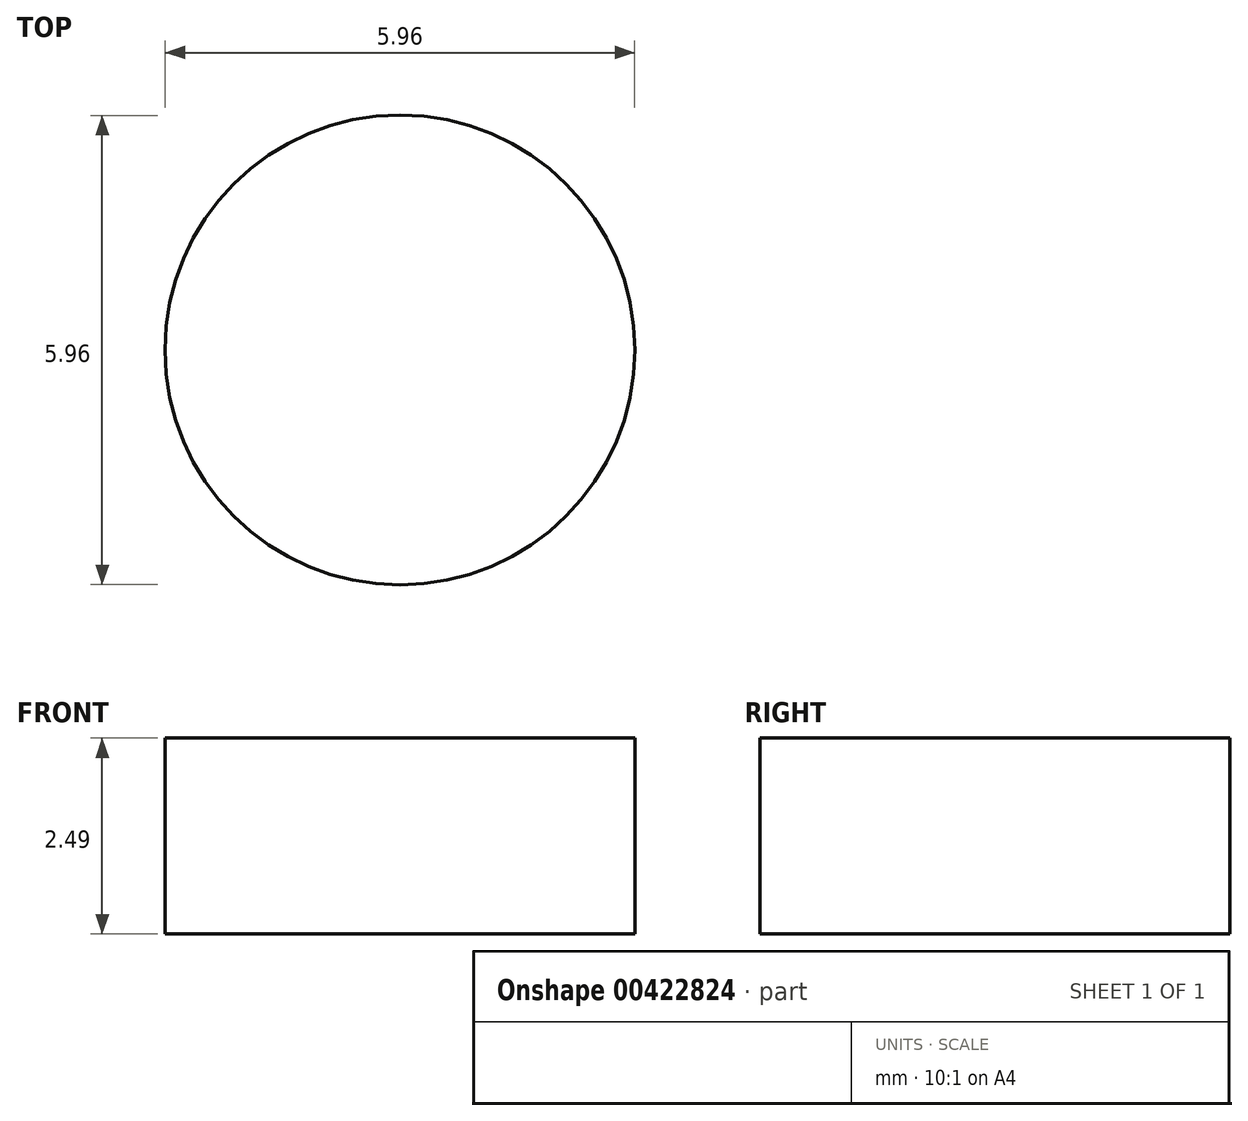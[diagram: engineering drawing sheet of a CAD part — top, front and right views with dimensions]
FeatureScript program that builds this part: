
annotation { "Feature Type Name" : "Feature", "Feature Type Description" : "" }
export const myFeature = defineFeature(function(context is Context, id is Id, definition is map)
    precondition{}
    {
        {
            var Q0;
            Q0=qCreatedBy(makeId("Top.planeOp"),FACE);
            var sketch = newSketch(context, id + "F0", { "sketchPlane" : qUnion([Q0])});
            skCircle(sketch, "E0", {"center": v(0, 0) * mm, "radius": 2.98 * mm});
            skSolve(sketch);
        }
        {
            var Q0;
            Q0 = qSketchRegion(id + "F0", true);
            extrude(context, id + "F1", {"entities" : qUnion([Q0]), "depth" : 2.5 * mm});
        }
    });
